# Revit family: Kamstrup_Ultraflow_54 резьбовые
name_source: partatom
category: Арматура трубопроводов
revit_build: Autodesk Revit 2016 (Build: 20150714_1515(x64)
units: mm (PartAtom-declared; Revit-internal decimal feet)

## family parameters
Всегда вертикально = Да
На основе рабочей плоскости = Нет
Общий = Нет
При загрузке вырезать с полостями = Нет
Размер круглого соединителя = Использовать диаметр
Тип детали = Встроенный датчик

## types (10) — shared parameters
150 = 150 мм
H1 = 55 мм
ID1 = Кабель 2.5 м
ID2 = Кабель 5 м
ID3 = Кабель 10 м
URL = https://www.kamstrup.com
Адрес = 141008, Московская обл., г. Мытищи, ул. Колпакова, 26
Изготовитель = ЗАО «Камструп»
Таблица_выбора = ultraflow 54H
Телефон = +7 495 545 00 01

## per-type parameters (varying)
| type | A | B1 | B2 | DN | DN_стенка | G | H2 | ID_гл | L | M | RN_стенка | видимость_H | видимость_неH |
| 65-5- CAHA | 8 мм | 37 мм | 32 мм | 15 мм | 17 мм | 20 мм | 86 мм | 1 мм | 110 мм | 55 мм | 9 мм | Да | Нет |
| 65-5- CAHD | 12 мм | 37 мм | 32 мм | 20 мм | 23 мм | 25 мм | 86 мм | 2 мм | 110 мм | 55 мм | 12 мм | Да | Нет |
| 65-5- CDHA | 12 мм | 37 мм | 32 мм | 15 мм | 17 мм | 20 мм | 86 мм | 3 мм | 130 мм | 65 мм | 9 мм | Да | Нет |
| 65-5- CDHC | 12 мм | 40 мм | 35 мм | 15 мм | 17 мм | 20 мм | 86 мм | 4 мм | 130 мм | 65 мм | 9 мм | Да | Нет |
| 65-5- CDHD | 8 мм | 37 мм | 32 мм | 20 мм | 23 мм | 25 мм | 86 мм | 5 мм | 165 мм | 83 мм | 12 мм | Да | Нет |
| 65-5- CDHF | 12 мм | 37 мм | 32 мм | 20 мм | 23 мм | 25 мм | 86 мм | 6 мм | 190 мм | 95 мм | 12 мм | Да | Нет |
| 65-5- CEHF | 12 мм | 40 мм | 35 мм | 20 мм | 23 мм | 25 мм | 86 мм | 7 мм | 190 мм | 95 мм | 12 мм | Да | Нет |
| 65-5- CGAG | 17 мм | 58 мм | 22 мм | 25 мм | 29 мм | 32 мм | 89 мм | 8 мм | 260 мм | 130 мм | 14 мм | Нет | Да |
| 65-5- CHAG | 17 мм | 58 мм | 22 мм | 25 мм | 29 мм | 32 мм | 89 мм | 9 мм | 260 мм | 130 мм | 14 мм | Нет | Да |
| 65-5- CJAJ | 21 мм | 65 мм | 31 мм | 40 мм | 46 мм | 50 мм | 86 мм | 10 мм | 300 мм | 150 мм | 23 мм | Нет | Да |

## geometry (parser evidence)
native form markers: Blend x2
no freeform markers — native parametric forms only
